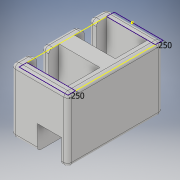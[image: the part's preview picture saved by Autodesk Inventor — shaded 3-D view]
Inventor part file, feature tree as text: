
AUTODESK INVENTOR PART (.ipt)
format: ipt  version: 2018.1 (Build 221171000, 171)  size: 239,104 bytes
history: native  units: in
note: dims shown in document units (in); Inventor stores cm internally (conversion verified against a paired STEP export)
features: sketch x12, extrude x9, fillet x2
ambient origin geometry x8: Origin, YZ Plane, XZ Plane, XY Plane, X Axis, Y Axis, Z Axis, Center Point
bodies: Solid1 (feature_tree)
feature tree (23):
  sketch  "Sketch1"  dims[d0=0.79in d1=0.79in]
  extrude  "Extrusion1"  Depth=0.79in
  extrude  "Extrusion2"  Depth=1.99in
  sketch  "Sketch3"  dims[d4=3.1in d5=0.0in d6=3.1in d7=0.0in]
  sketch  "Sketch4"  dims[d8=0.4in d9=0.0in d10=0.25in]
  extrude  "Extrusion3"  Depth=3.1in TaperAngle=0.0deg
  sketch  "Sketch6"  dims[d14=1.34in d15=1.05in]
  extrude  "Extrusion4"  Depth=0.25in
  sketch  "Sketch8"  dims[d20=0.1in d21=0.0in d22=1.25in d23=0.0in]
  extrude  "Extrusion5"  Depth=0.25in TaperAngle=0.0deg
  extrude  "Extrusion6"  Depth=1.05in
  extrude  "Extrusion7"  Depth=1.05in TaperAngle=0.0deg
  sketch  "Sketch11"  dims[d31=0.125in]
  extrude  "Extrusion8"  Depth=1.25in TaperAngle=0.0deg
  extrude  "Extrusion9"  Depth=0.4in
  fillet  "Fillet1"  Radius=1.25in
  fillet  "Fillet2"  Radius=1.25in
  sketch  "Sketch2"  dims[d2=1.19in d3=1.99in]
  sketch  "Sketch5"  dims[d11=0.25in d12=0.25in d13=0.0in]
  sketch  "Sketch7"  dims[d16=1.34in d17=1.05in d18=0.1in d19=0.0in]
  sketch  "Sketch9"  dims[d24=0.4in d25=0.4in d26=1.25in d27=0.0in d28=1.25in d29=0.0in]
  sketch  "Sketch10"  dims[d30=0.125in]
  sketch  "Sketch12"
